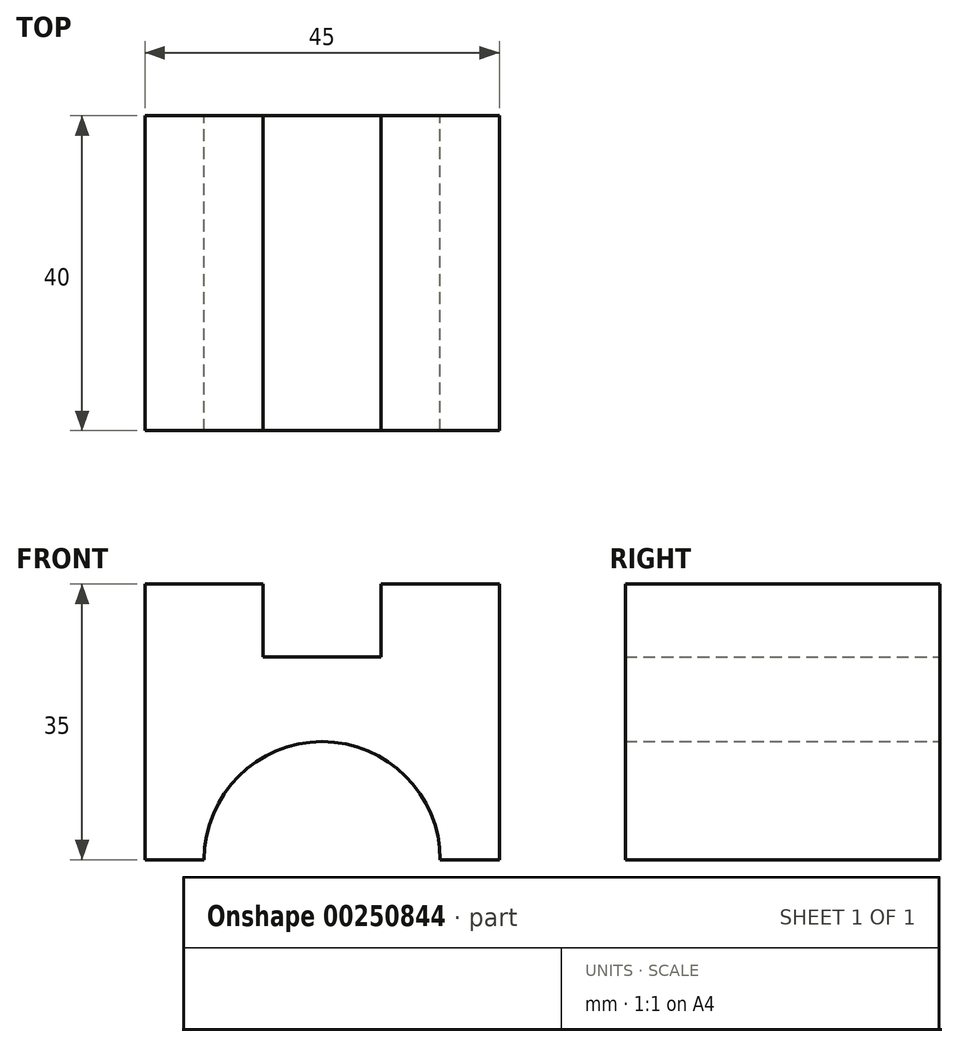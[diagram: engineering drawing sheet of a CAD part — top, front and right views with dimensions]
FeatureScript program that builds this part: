
annotation { "Feature Type Name" : "Feature", "Feature Type Description" : "" }
export const myFeature = defineFeature(function(context is Context, id is Id, definition is map)
    precondition{}
    {
        {
            var Q0;
            Q0=qCreatedBy(makeId("Front.planeOp"),FACE);
            var sketch = newSketch(context, id + "F0", { "sketchPlane" : qUnion([Q0])});
            skLineSegment(sketch, "E0", {"start": v(0, 0) * mm, "end": v(0, 35) * mm});
            skLineSegment(sketch, "E1", {"start": v(0, 35) * mm, "end": v(15, 35) * mm});
            skLineSegment(sketch, "E2", {"start": v(15, 35) * mm, "end": v(15, 25.79) * mm});
            skLineSegment(sketch, "E3", {"start": v(15, 25.79) * mm, "end": v(30, 25.79) * mm});
            skLineSegment(sketch, "E4", {"start": v(30, 25.79) * mm, "end": v(30, 35) * mm});
            skLineSegment(sketch, "E5", {"start": v(30, 35) * mm, "end": v(45, 35) * mm});
            skLineSegment(sketch, "E6", {"start": v(45, 35) * mm, "end": v(45, 0) * mm});
            skLineSegment(sketch, "E7", {"start": v(0, 0) * mm, "end": v(45, 0) * mm});
            skCircle(sketch, "E8", {"center": v(22.5, 0) * mm, "radius": 15 * mm});
            skSolve(sketch);
        }
        {
            var Q0;
            {var subQ5=sQuery(id+"F0.wireOp",EDGE,"E0");Q0=makeQuery(id+"F0.imprint","IMPRINT",FACE,{"disambiguationData":[TD([[makeQuery(id+"F0.imprint","IMPRINT",EDGE,{"derivedFrom":subQ5}),-1.0]])]});}
            extrude(context, id + "F1", {"entities" : qUnion([Q0]), "depth" : 40 * mm});
        }
    });
